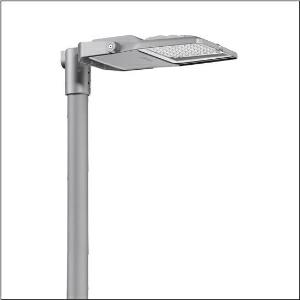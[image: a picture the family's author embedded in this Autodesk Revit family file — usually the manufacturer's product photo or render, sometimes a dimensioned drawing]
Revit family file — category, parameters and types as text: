
# Revit family: floodlight_fl_21_iq_mini___pl33t_5xa7771d2f3a_c3c2
name_source: partatom
category: Lighting Fixtures
units: mm (PartAtom-declared; Revit-internal decimal feet)

## family parameters
Cut with Voids When Loaded = No
Host = Face
Light Source = No
Part Type = Normal
Room Calculation Point = No
Round Connector Dimension = Use Diameter
Shared = No

## types (1)
- --- (1 x LED, 17620 lm, 143 W, 3000K)
    Apparent Load = 143 VA
    CIE Flux Codes = 26 75 99 100 100
    Color Rendering = 70
    Color Temperature = 3000K
    Default Elevation = 1800 mm
    Description = Floodlight FL 21 iQ mini, floodlight, primary light control with lens, of PMMA, primary optical cover: protective disc, of toughened safety glass, transparent, light distribution: PL33T, light emission: direct distribution, installation type: surface-mounted, LED, High Power LED, rated luminous flux: 17.620lm, luminous efficacy: 123lm/W, light colour: 730, colour temperature: 3000K, control: Auto-Match, Temp-Guard, Lumen-Switch, Night-Set, Smart-Wire, Light-Fading, Desk-Remote (wireless, voltage-free reading and setting of iQ features in the workshop via application-optimized NFC function/RFID function), optimised constant luminous flux control (CLO 2.0), with terminal, 6-pole, mains connection: 220..240V, AC, 50/60Hz, start of lifetime: 143W, end of service life: 152W, reduction: 61W, luminaire housing, of diecast aluminium, powder-coated, Siteco® metallic grey (DB 702S), corrosivity category C5 mid according to DIN EN ISO 12944, sealing non-destructively replaceable, please order mast flange separately, mast bracket, of steel, galvanised, powder-coated, Siteco® metallic grey (DB 702S), protection rating (complete): IP66, insulation class (complete): insulation class II (safety insulation), certification: CE, ENEC, VDE, protection symbol: D, impact resistance: IK08, permissible operating ambient temperature: -40..+40°C, permissible operating ambient temperature for outdoor applications: -40..+50°C, standard: DIN EN 12944, LABS conformity tested according to VDMA 24364:2018-05, packaging unit: 1 piece

Light Distribution: PL33T
    Height = 70 mm
    Lamp = 1 x LED
    Lamp Light Flux = 17620 lm
    Lamp Power = 143 W
    Lamp count = 1
    Length = 485 mm
    Luminous efficacy = 123 lm/W
    Manufacturer = Siteco
    ModVariant = No
    Model = 5XA7771D2F3A
    Number of Poles = 1
    OnlyDefault = Yes
    Power Factor = 1
    Product Name = Floodlight FL 21 iQ mini | PL33T
    Product group = floodlight | pylon annexe
    ProductGroupID = 6200
    Protection Class = Protection class II
    Protection Degree = IP 66
    RLX_Detail_Level = 1
    RLX_Emergency_Light_Flux = 0 lm
    RLX_Emergency_Type = 0
    RLX_Emergency_Type_DB = No
    RlxData = <blob elided: 101489 chars, md5=0d29dd1d>
    Socket = socket
    Standby Power = 0 W
    System Light Flux = 17620 lm
    System Power = 143 W
    Type Comments = factory setting: luminous flux: 100 % | dim-lin: 254 | 730 mA
    Type Image = l_1007125.jpg
    URL = http://relux.com
    VarID = @adj_099355
    Voltage = 0 V
    Weight = 0.00 kg
    Width = 337 mm

## geometry (parser evidence)
native form markers: Blend x4, Sweep x11
no freeform markers — native parametric forms only
